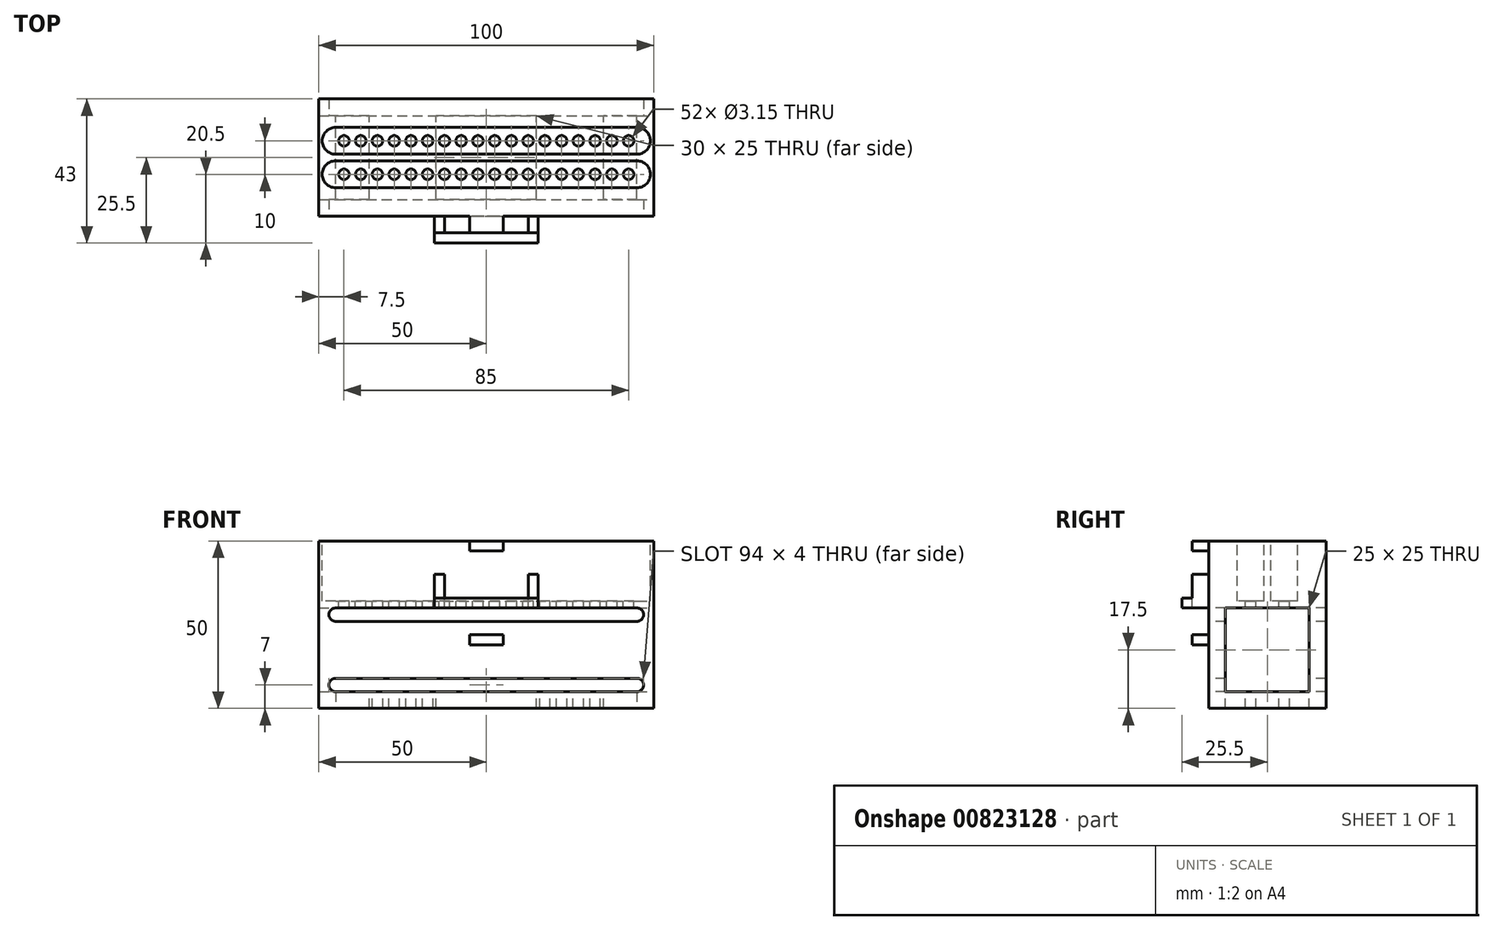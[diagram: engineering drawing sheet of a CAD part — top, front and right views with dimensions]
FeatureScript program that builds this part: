
annotation { "Feature Type Name" : "Feature", "Feature Type Description" : "" }
export const myFeature = defineFeature(function(context is Context, id is Id, definition is map)
    precondition{}
    {
        {
            var Q0;
            Q0=qCreatedBy(makeId("Top.planeOp"),FACE);
            var sketch = newSketch(context, id + "F0", { "sketchPlane" : qUnion([Q0])});
            skLineSegment(sketch, "E0.bottom", {"start": v(50, 17.5) * mm, "end": v(-50, 17.5) * mm});
            skLineSegment(sketch, "E0.top", {"start": v(50, -17.5) * mm, "end": v(-50, -17.5) * mm});
            skLineSegment(sketch, "E0.left", {"start": v(50, 17.5) * mm, "end": v(50, -17.5) * mm});
            skLineSegment(sketch, "E0.right", {"start": v(-50, 17.5) * mm, "end": v(-50, -17.5) * mm});
            skPoint(sketch, "E0.middle", {"position": v(0, 0) * mm});
            skSolve(sketch);
        }
        {
            var Q0;
            Q0 = qSketchRegion(id + "F0", true);
            extrude(context, id + "F1", {"entities" : qUnion([Q0]), "depth" : 50 * mm, "offsetDistance" : 25 * mm});
        }
        {
            var Q0;
            Q0=makeQuery(id+"F1.opExtrude","SWEPT_FACE",FACE,{"disambiguationData":[OSD([sQuery(id+"F0.wireOp",EDGE,"E0.top")])]});
            var sketch = newSketch(context, id + "F2", { "sketchPlane" : qUnion([Q0])});
            skLineSegment(sketch, "E1", {"start": v(-45, 9) * mm, "end": v(0, 9) * mm});
            skLineSegment(sketch, "E2", {"start": v(-45, 5) * mm, "end": v(0, 5) * mm});
            skLineSegment(sketch, "E3", {"start": v(0, 0) * mm, "end": v(0, 34.25) * mm, "construction": true});
            skPoint(sketch, "E3.endSnap0", {"position": v(0, 50) * mm});
            skArc(sketch, "E4", {"start": v(-45, 5) * mm, "mid": v(-47, 7) * mm, "end": v(-45, 9) * mm});
            skLineSegment(sketch, "E5.MirrorCS", {"start": v(45, 5) * mm, "end": v(0, 5) * mm});
            skLineSegment(sketch, "E6.MirrorCS", {"start": v(45, 9) * mm, "end": v(0, 9) * mm});
            skArc(sketch, "E7.MirrorCS", {"start": v(45, 5) * mm, "mid": v(47, 7) * mm, "end": v(45, 9) * mm});
            skPoint(sketch, "E8.start.orphan", {"position": v(0, 9.86) * mm});
            skLineSegment(sketch, "E9", {"start": v(0, 17.5) * mm, "end": v(12.68, 17.5) * mm, "construction": true});
            skLineSegment(sketch, "E10.MirrorCS", {"start": v(45, 26) * mm, "end": v(0, 26) * mm});
            skLineSegment(sketch, "E11.MirrorCS", {"start": v(45, 30) * mm, "end": v(0, 30) * mm});
            skLineSegment(sketch, "E12.MirrorCS", {"start": v(-45, 26) * mm, "end": v(0, 26) * mm});
            skLineSegment(sketch, "E13.MirrorCS", {"start": v(-45, 30) * mm, "end": v(0, 30) * mm});
            skArc(sketch, "E14.MirrorCS", {"start": v(45, 30) * mm, "mid": v(47, 28) * mm, "end": v(45, 26) * mm});
            skArc(sketch, "E15.MirrorCS", {"start": v(-45, 30) * mm, "mid": v(-47, 28) * mm, "end": v(-45, 26) * mm});
            skSolve(sketch);
        }
        {
            var Q0;
            Q0 = qSketchRegion(id + "F2", true);
            extrude(context, id + "F3", {"entities" : qUnion([Q0]), "operationType" : NewBodyOperationType.REMOVE, "endBound" : BoundingType.THROUGH_ALL, "oppositeDirection" : true, "depth" : 25 * mm, "offsetDistance" : 25 * mm});
        }
        {
            var Q0;
            Q0=makeQuery(id+"F1.opExtrude","CAP_FACE",FACE,{"disambiguationData":[OSD([sQuery(id+"F0.wireOp",EDGE,"E0.bottom"),sQuery(id+"F0.wireOp",EDGE,"E0.top"),sQuery(id+"F0.wireOp",EDGE,"E0.left"),sQuery(id+"F0.wireOp",EDGE,"E0.right")])],"isStart":true});
            var sketch = newSketch(context, id + "F4", { "sketchPlane" : qUnion([Q0])});
            skLineSegment(sketch, "E16.bottom", {"start": v(45, 12.5) * mm, "end": v(-45, 12.5) * mm});
            skLineSegment(sketch, "E16.top", {"start": v(45, -12.5) * mm, "end": v(-45, -12.5) * mm});
            skLineSegment(sketch, "E16.left", {"start": v(45, 12.5) * mm, "end": v(45, -12.5) * mm});
            skLineSegment(sketch, "E16.right", {"start": v(-45, 12.5) * mm, "end": v(-45, -12.5) * mm});
            skPoint(sketch, "E16.middle", {"position": v(0, 0) * mm});
            skSolve(sketch);
        }
        {
            var Q0;
            Q0 = qSketchRegion(id + "F4", true);
            extrude(context, id + "F5", {"entities" : qUnion([Q0]), "operationType" : NewBodyOperationType.REMOVE, "oppositeDirection" : true, "depth" : 30 * mm, "offsetDistance" : 25 * mm});
        }
        {
            var Q0;
            Q0=makeQuery(id+"F1.opExtrude","CAP_FACE",FACE,{"disambiguationData":[OSD([sQuery(id+"F0.wireOp",EDGE,"E0.bottom"),sQuery(id+"F0.wireOp",EDGE,"E0.top"),sQuery(id+"F0.wireOp",EDGE,"E0.left"),sQuery(id+"F0.wireOp",EDGE,"E0.right")])],"isStart":false});
            var sketch = newSketch(context, id + "F6", { "sketchPlane" : qUnion([Q0])});
            skCircle(sketch, "E17", {"center": v(-42.5, 5) * mm, "radius": 1.58 * mm});
            skCircle(sketch, "E18.MirrorC", {"center": v(-42.5, -5) * mm, "radius": 1.58 * mm});
            skCircle(sketch, "E19.1.0.0", {"center": v(-37.5, 5) * mm, "radius": 1.58 * mm});
            skCircle(sketch, "E19.1.0.1", {"center": v(-37.5, -5) * mm, "radius": 1.58 * mm});
            skCircle(sketch, "E19.2.0.0", {"center": v(-32.5, 5) * mm, "radius": 1.58 * mm});
            skCircle(sketch, "E19.2.0.1", {"center": v(-32.5, -5) * mm, "radius": 1.58 * mm});
            skCircle(sketch, "E19.3.0.0", {"center": v(-27.5, 5) * mm, "radius": 1.58 * mm});
            skCircle(sketch, "E19.3.0.1", {"center": v(-27.5, -5) * mm, "radius": 1.58 * mm});
            skCircle(sketch, "E19.4.0.0", {"center": v(-22.5, 5) * mm, "radius": 1.58 * mm});
            skCircle(sketch, "E19.4.0.1", {"center": v(-22.5, -5) * mm, "radius": 1.58 * mm});
            skCircle(sketch, "E19.5.0.0", {"center": v(-17.5, 5) * mm, "radius": 1.58 * mm});
            skCircle(sketch, "E19.5.0.1", {"center": v(-17.5, -5) * mm, "radius": 1.58 * mm});
            skCircle(sketch, "E19.6.0.0", {"center": v(-12.5, 5) * mm, "radius": 1.58 * mm});
            skCircle(sketch, "E19.6.0.1", {"center": v(-12.5, -5) * mm, "radius": 1.58 * mm});
            skCircle(sketch, "E19.7.0.0", {"center": v(-7.5, 5) * mm, "radius": 1.58 * mm});
            skCircle(sketch, "E19.7.0.1", {"center": v(-7.5, -5) * mm, "radius": 1.58 * mm});
            skCircle(sketch, "E19.8.0.0", {"center": v(-2.5, 5) * mm, "radius": 1.58 * mm});
            skCircle(sketch, "E19.8.0.1", {"center": v(-2.5, -5) * mm, "radius": 1.58 * mm});
            skCircle(sketch, "E19.9.0.0", {"center": v(2.5, 5) * mm, "radius": 1.58 * mm});
            skCircle(sketch, "E19.9.0.1", {"center": v(2.5, -5) * mm, "radius": 1.58 * mm});
            skCircle(sketch, "E19.10.0.0", {"center": v(7.5, 5) * mm, "radius": 1.58 * mm});
            skCircle(sketch, "E19.10.0.1", {"center": v(7.5, -5) * mm, "radius": 1.58 * mm});
            skCircle(sketch, "E19.11.0.0", {"center": v(12.5, 5) * mm, "radius": 1.58 * mm});
            skCircle(sketch, "E19.11.0.1", {"center": v(12.5, -5) * mm, "radius": 1.58 * mm});
            skCircle(sketch, "E19.12.0.0", {"center": v(17.5, 5) * mm, "radius": 1.58 * mm});
            skCircle(sketch, "E19.12.0.1", {"center": v(17.5, -5) * mm, "radius": 1.58 * mm});
            skCircle(sketch, "E19.13.0.0", {"center": v(22.5, 5) * mm, "radius": 1.58 * mm});
            skCircle(sketch, "E19.13.0.1", {"center": v(22.5, -5) * mm, "radius": 1.58 * mm});
            skCircle(sketch, "E19.14.0.0", {"center": v(27.5, 5) * mm, "radius": 1.58 * mm});
            skCircle(sketch, "E19.14.0.1", {"center": v(27.5, -5) * mm, "radius": 1.58 * mm});
            skCircle(sketch, "E19.15.0.0", {"center": v(32.5, 5) * mm, "radius": 1.58 * mm});
            skCircle(sketch, "E19.15.0.1", {"center": v(32.5, -5) * mm, "radius": 1.58 * mm});
            skCircle(sketch, "E19.16.0.0", {"center": v(37.5, 5) * mm, "radius": 1.58 * mm});
            skCircle(sketch, "E19.16.0.1", {"center": v(37.5, -5) * mm, "radius": 1.58 * mm});
            skCircle(sketch, "E19.17.0.0", {"center": v(42.5, 5) * mm, "radius": 1.58 * mm});
            skCircle(sketch, "E19.17.0.1", {"center": v(42.5, -5) * mm, "radius": 1.58 * mm});
            skLineSegment(sketch, "E19.direction1", {"start": v(-42.5, -5) * mm, "end": v(-37.5, -5) * mm, "construction": true});
            skSolve(sketch);
        }
        {
            var Q0;
            Q0 = qSketchRegion(id + "F6", true);
            extrude(context, id + "F7", {"entities" : qUnion([Q0]), "operationType" : NewBodyOperationType.REMOVE, "endBound" : BoundingType.THROUGH_ALL, "oppositeDirection" : true, "depth" : 25 * mm, "offsetDistance" : 25 * mm});
        }
        {
            var Q0;
            Q0=makeQuery(id+"F1.opExtrude","CAP_FACE",FACE,{"disambiguationData":[OSD([sQuery(id+"F0.wireOp",EDGE,"E0.bottom"),sQuery(id+"F0.wireOp",EDGE,"E0.top"),sQuery(id+"F0.wireOp",EDGE,"E0.left"),sQuery(id+"F0.wireOp",EDGE,"E0.right")])],"isStart":false});
            var sketch = newSketch(context, id + "F8", { "sketchPlane" : qUnion([Q0])});
            skLineSegment(sketch, "E20", {"start": v(-45, 9) * mm, "end": v(45, 9) * mm});
            skLineSegment(sketch, "E21", {"start": v(-45, 1) * mm, "end": v(45, 1) * mm});
            skLineSegment(sketch, "E22", {"start": v(-42.5, 5) * mm, "end": v(-42.5, 9) * mm, "construction": true});
            skLineSegment(sketch, "E23", {"start": v(-37.5, 5) * mm, "end": v(-37.5, 1) * mm, "construction": true});
            skArc(sketch, "E24", {"start": v(-45, 1) * mm, "mid": v(-49, 5) * mm, "end": v(-45, 9) * mm});
            skArc(sketch, "E25", {"start": v(45, 1) * mm, "mid": v(49, 5) * mm, "end": v(45, 9) * mm});
            skLineSegment(sketch, "E26.MirrorCS", {"start": v(-45, -9) * mm, "end": v(45, -9) * mm});
            skLineSegment(sketch, "E27.MirrorCS", {"start": v(-45, -1) * mm, "end": v(45, -1) * mm});
            skArc(sketch, "E28.MirrorCS", {"start": v(-45, -1) * mm, "mid": v(-49, -5) * mm, "end": v(-45, -9) * mm});
            skArc(sketch, "E29.MirrorCS", {"start": v(45, -1) * mm, "mid": v(49, -5) * mm, "end": v(45, -9) * mm});
            skSolve(sketch);
        }
        {
            var Q0;
            Q0 = qSketchRegion(id + "F8", true);
            extrude(context, id + "F9", {"entities" : qUnion([Q0]), "operationType" : NewBodyOperationType.REMOVE, "oppositeDirection" : true, "depth" : 18 * mm, "offsetDistance" : 25 * mm});
        }
        {
            var Q0;
            Q0=makeQuery(id+"F5.boolean.opBoolean","COPY",FACE,{"disambiguationData":[TD([makeQuery(id+"F3.boolean.opBoolean","COPY",FACE,{"derivedFrom":makeQuery(id+"F3.opExtrude","SWEPT_FACE",FACE,{"disambiguationData":[OSD([sQuery(id+"F2.wireOp",EDGE,"E2"),sQuery(id+"F2.wireOp",EDGE,"E5.MirrorCS")])]})})])],"derivedFrom":makeQuery(id+"F5.opExtrude","SWEPT_FACE",FACE,{"disambiguationData":[OSD([sQuery(id+"F4.wireOp",EDGE,"E16.top")])]})});
            var sketch = newSketch(context, id + "F10", { "sketchPlane" : qUnion([Q0])});
            skLineSegment(sketch, "E30.bottom", {"start": v(-35, 0) * mm, "end": v(-15, 0) * mm});
            skLineSegment(sketch, "E30.top", {"start": v(-35, 5) * mm, "end": v(-15, 5) * mm});
            skLineSegment(sketch, "E30.left", {"start": v(-35, 0) * mm, "end": v(-35, 5) * mm});
            skLineSegment(sketch, "E30.right", {"start": v(-15, 0) * mm, "end": v(-15, 5) * mm});
            skLineSegment(sketch, "E31.MirrorCS", {"start": v(35, 0) * mm, "end": v(15, 0) * mm});
            skLineSegment(sketch, "E32.MirrorCS", {"start": v(15, 0) * mm, "end": v(15, 5) * mm});
            skLineSegment(sketch, "E33.MirrorCS", {"start": v(35, 5) * mm, "end": v(15, 5) * mm});
            skLineSegment(sketch, "E34.MirrorCS", {"start": v(35, 0) * mm, "end": v(35, 5) * mm});
            skSolve(sketch);
        }
        {
            var Q0;
            Q0 = qSketchRegion(id + "F10", true);
            extrude(context, id + "F11", {"entities" : qUnion([Q0]), "operationType" : NewBodyOperationType.ADD, "depth" : 25 * mm, "offsetDistance" : 25 * mm});
        }
        {
            var Q0;
            Q0=makeQuery(id+"F1.opExtrude","SWEPT_FACE",FACE,{"disambiguationData":[OSD([sQuery(id+"F0.wireOp",EDGE,"E0.left")])]});
            var sketch = newSketch(context, id + "F12", { "sketchPlane" : qUnion([Q0])});
            skLineSegment(sketch, "E35.bottom", {"start": v(-12.5, 5) * mm, "end": v(12.5, 5) * mm});
            skLineSegment(sketch, "E35.top", {"start": v(-12.5, 30) * mm, "end": v(12.5, 30) * mm});
            skLineSegment(sketch, "E35.left", {"start": v(-12.5, 5) * mm, "end": v(-12.5, 30) * mm});
            skLineSegment(sketch, "E35.right", {"start": v(12.5, 5) * mm, "end": v(12.5, 30) * mm});
            skSolve(sketch);
        }
        {
            var Q0;
            Q0 = qSketchRegion(id + "F12", true);
            extrude(context, id + "F13", {"entities" : qUnion([Q0]), "operationType" : NewBodyOperationType.REMOVE, "endBound" : BoundingType.THROUGH_ALL, "oppositeDirection" : true, "depth" : 25 * mm, "offsetDistance" : 25 * mm});
        }
        {
            var Q0;
            Q0=makeQuery(id+"F1.opExtrude","SWEPT_FACE",FACE,{"disambiguationData":[OSD([sQuery(id+"F0.wireOp",EDGE,"E0.top")])]});
            var sketch = newSketch(context, id + "F14", { "sketchPlane" : qUnion([Q0])});
            skLineSegment(sketch, "E36.bottom", {"start": v(-15.5, 30) * mm, "end": v(-12.5, 30) * mm});
            skLineSegment(sketch, "E36.top", {"start": v(-15.5, 40) * mm, "end": v(-12.5, 40) * mm});
            skLineSegment(sketch, "E36.left", {"start": v(-15.5, 30) * mm, "end": v(-15.5, 40) * mm});
            skLineSegment(sketch, "E36.right", {"start": v(-12.5, 30) * mm, "end": v(-12.5, 40) * mm});
            skLineSegment(sketch, "E37.bottom", {"start": v(12.5, 30) * mm, "end": v(15.5, 30) * mm});
            skLineSegment(sketch, "E37.top", {"start": v(12.5, 40) * mm, "end": v(15.5, 40) * mm});
            skLineSegment(sketch, "E37.left", {"start": v(12.5, 30) * mm, "end": v(12.5, 40) * mm});
            skLineSegment(sketch, "E37.right", {"start": v(15.5, 30) * mm, "end": v(15.5, 40) * mm});
            skLineSegment(sketch, "E38.bottom", {"start": v(-5, 50) * mm, "end": v(5, 50) * mm});
            skLineSegment(sketch, "E38.top", {"start": v(-5, 47) * mm, "end": v(5, 47) * mm});
            skLineSegment(sketch, "E38.left", {"start": v(-5, 50) * mm, "end": v(-5, 47) * mm});
            skLineSegment(sketch, "E38.right", {"start": v(5, 50) * mm, "end": v(5, 47) * mm});
            skLineSegment(sketch, "E39.bottom", {"start": v(-5, 22) * mm, "end": v(5, 22) * mm});
            skLineSegment(sketch, "E39.top", {"start": v(-5, 19) * mm, "end": v(5, 19) * mm});
            skLineSegment(sketch, "E39.left", {"start": v(-5, 22) * mm, "end": v(-5, 19) * mm});
            skLineSegment(sketch, "E39.right", {"start": v(5, 22) * mm, "end": v(5, 19) * mm});
            skLineSegment(sketch, "E40", {"start": v(-50, 35.34) * mm, "end": v(-15.5, 35.34) * mm, "construction": true});
            skLineSegment(sketch, "E41", {"start": v(15.5, 35) * mm, "end": v(50, 35) * mm, "construction": true});
            skLineSegment(sketch, "E42", {"start": v(-12.5, 30) * mm, "end": v(-5, 22) * mm, "construction": true});
            skLineSegment(sketch, "E43", {"start": v(5, 47) * mm, "end": v(12.5, 40) * mm, "construction": true});
            skLineSegment(sketch, "E44", {"start": v(-12.5, 40) * mm, "end": v(-5, 47) * mm, "construction": true});
            skLineSegment(sketch, "E45", {"start": v(5, 22) * mm, "end": v(12.5, 30) * mm, "construction": true});
            skSolve(sketch);
        }
        {
            var Q0;
            Q0 = qSketchRegion(id + "F14", true);
            extrude(context, id + "F15", {"entities" : qUnion([Q0]), "operationType" : NewBodyOperationType.ADD, "depth" : 5 * mm, "offsetDistance" : 25 * mm});
        }
        {
            var Q0;
            {var subQ4=makeQuery(id+"F3.boolean.opBoolean","COPY",FACE,{"derivedFrom":makeQuery(id+"F3.opExtrude","SWEPT_FACE",FACE,{"disambiguationData":[OSD([sQuery(id+"F2.wireOp",EDGE,"E2"),sQuery(id+"F2.wireOp",EDGE,"E5.MirrorCS")])]})});Q0=makeQuery(id+"F11.boolean.opBoolean","MERGE",FACE,{"derivedFrom":[makeQuery(id+"F5.boolean.opBoolean","SPLIT",FACE,{"disambiguationData":[TD([makeQuery(id+"F1.opExtrude","SWEPT_FACE",FACE,{"disambiguationData":[OSD([sQuery(id+"F0.wireOp",EDGE,"E0.top")])]})])],"derivedFrom":subQ4}),makeQuery(id+"F5.boolean.opBoolean","SPLIT",FACE,{"disambiguationData":[TD([makeQuery(id+"F1.opExtrude","SWEPT_FACE",FACE,{"disambiguationData":[OSD([sQuery(id+"F0.wireOp",EDGE,"E0.bottom")])]})])],"derivedFrom":subQ4}),makeQuery(id+"F11.opExtrude","SWEPT_FACE",FACE,{"disambiguationData":[OSD([sQuery(id+"F10.wireOp",EDGE,"E30.top")])]}),makeQuery(id+"F11.opExtrude","SWEPT_FACE",FACE,{"disambiguationData":[OSD([sQuery(id+"F10.wireOp",EDGE,"E33.MirrorCS")])]})]});}
            var sketch = newSketch(context, id + "F16", { "sketchPlane" : qUnion([Q0])});
            skCircle(sketch, "E46", {"center": v(-32.5, 5) * mm, "radius": 1.58 * mm});
            skCircle(sketch, "E47", {"center": v(-27.5, 5) * mm, "radius": 1.58 * mm});
            skCircle(sketch, "E48", {"center": v(-22.5, 5) * mm, "radius": 1.58 * mm});
            skCircle(sketch, "E49", {"center": v(-17.5, 5) * mm, "radius": 1.58 * mm});
            skCircle(sketch, "E50", {"center": v(-32.5, -5) * mm, "radius": 1.58 * mm});
            skCircle(sketch, "E51", {"center": v(-22.5, -5) * mm, "radius": 1.58 * mm});
            skCircle(sketch, "E52", {"center": v(-27.5, -5) * mm, "radius": 1.58 * mm});
            skCircle(sketch, "E53", {"center": v(-17.5, -5) * mm, "radius": 1.58 * mm});
            skCircle(sketch, "E54", {"center": v(17.5, 5) * mm, "radius": 1.58 * mm});
            skCircle(sketch, "E55", {"center": v(17.5, -5) * mm, "radius": 1.58 * mm});
            skCircle(sketch, "E56", {"center": v(22.5, 5) * mm, "radius": 1.58 * mm});
            skCircle(sketch, "E57", {"center": v(22.5, -5) * mm, "radius": 1.58 * mm});
            skCircle(sketch, "E58", {"center": v(27.5, 5) * mm, "radius": 1.58 * mm});
            skCircle(sketch, "E59", {"center": v(27.5, -5) * mm, "radius": 1.58 * mm});
            skCircle(sketch, "E60", {"center": v(32.5, 5) * mm, "radius": 1.58 * mm});
            skCircle(sketch, "E61", {"center": v(32.5, -5) * mm, "radius": 1.58 * mm});
            skSolve(sketch);
        }
        {
            var Q0;
            Q0 = qSketchRegion(id + "F16", true);
            extrude(context, id + "F17", {"entities" : qUnion([Q0]), "operationType" : NewBodyOperationType.REMOVE, "endBound" : BoundingType.THROUGH_ALL, "oppositeDirection" : true, "depth" : 25 * mm, "offsetDistance" : 25 * mm});
        }
        {
            var Q0;
            Q0=makeQuery(id+"F15.opExtrude","CAP_FACE",FACE,{"disambiguationData":[OSD([sQuery(id+"F14.wireOp",EDGE,"E36.bottom"),sQuery(id+"F14.wireOp",EDGE,"E36.top"),sQuery(id+"F14.wireOp",EDGE,"E36.left"),sQuery(id+"F14.wireOp",EDGE,"E36.right")])],"isStart":false});
            var sketch = newSketch(context, id + "F18", { "sketchPlane" : qUnion([Q0])});
            skLineSegment(sketch, "E62.bottom", {"start": v(-15.5, 33) * mm, "end": v(15.5, 33) * mm});
            skLineSegment(sketch, "E62.top", {"start": v(-15.5, 30) * mm, "end": v(15.5, 30) * mm});
            skLineSegment(sketch, "E62.left", {"start": v(-15.5, 33) * mm, "end": v(-15.5, 30) * mm});
            skLineSegment(sketch, "E62.right", {"start": v(15.5, 33) * mm, "end": v(15.5, 30) * mm});
            skSolve(sketch);
        }
        {
            var Q0;
            Q0 = qSketchRegion(id + "F18", true);
            extrude(context, id + "F19", {"entities" : qUnion([Q0]), "operationType" : NewBodyOperationType.ADD, "depth" : 3 * mm, "offsetDistance" : 25 * mm});
        }
    });
